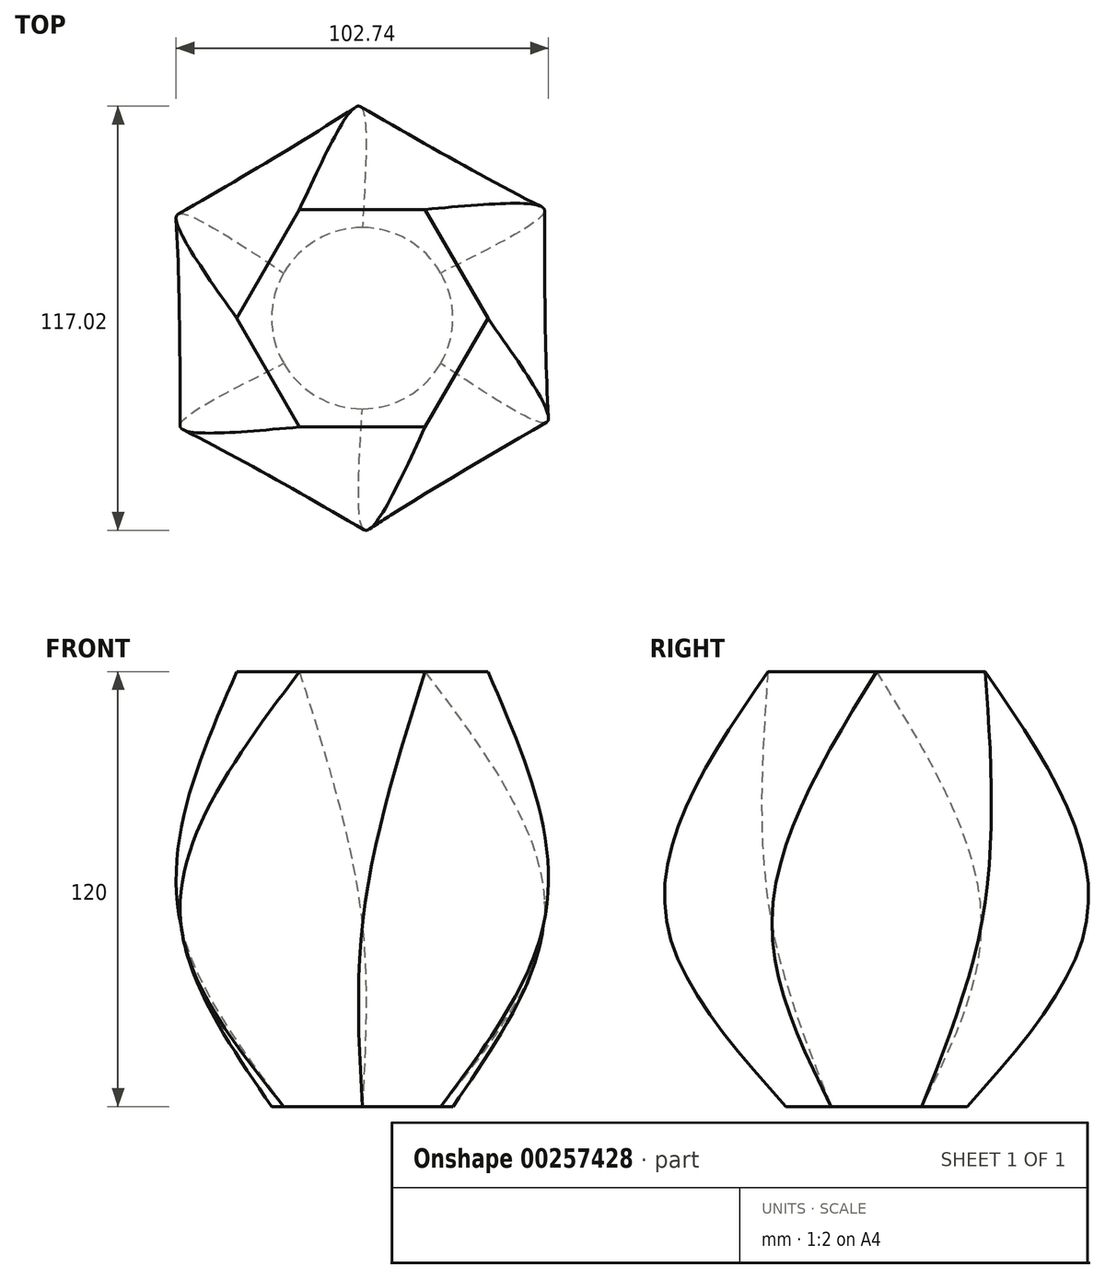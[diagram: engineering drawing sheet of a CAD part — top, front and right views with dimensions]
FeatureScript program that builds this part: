
annotation { "Feature Type Name" : "Feature", "Feature Type Description" : "" }
export const myFeature = defineFeature(function(context is Context, id is Id, definition is map)
    precondition{}
    {
        {
            var Q0;
            Q0=qCreatedBy(makeId("Top.planeOp"),FACE);
            cPlane(context, id + "F0", {"entities" : qUnion([Q0]), "cplaneType" : CPlaneType.OFFSET, "offset" : 50 * mm, "width" : 150 * mm, "height" : 150 * mm});
        }
        {
            var Q0;
            Q0=qCreatedBy(makeId("Top.planeOp"),FACE);
            cPlane(context, id + "F1", {"entities" : qUnion([Q0]), "cplaneType" : CPlaneType.OFFSET, "offset" : 120 * mm, "width" : 150 * mm, "height" : 150 * mm});
        }
        {
            var Q0;
            Q0=qCreatedBy(id+"F1.planeOp",FACE);
            var sketch = newSketch(context, id + "F2", { "sketchPlane" : qUnion([Q0])});
            skLineSegment(sketch, "E0", {"start": v(0, 52.7) * mm, "end": v(0, -45.29) * mm, "construction": true});
            skLineSegment(sketch, "E1", {"start": v(-54.44, 0) * mm, "end": v(51.9, 0) * mm, "construction": true});
            skCircle(sketch, "E2.cCircle", {"center": v(0, 0) * mm, "radius": 30 * mm, "construction": true});
            skLineSegment(sketch, "E2.0", {"start": v(17.32, -30) * mm, "end": v(-17.32, -30) * mm});
            skLineSegment(sketch, "E2.1", {"start": v(-17.32, -30) * mm, "end": v(-34.64, 0) * mm});
            skLineSegment(sketch, "E2.2", {"start": v(-34.64, 0) * mm, "end": v(-17.32, 30) * mm});
            skLineSegment(sketch, "E2.3", {"start": v(-17.32, 30) * mm, "end": v(17.32, 30) * mm});
            skLineSegment(sketch, "E2.4", {"start": v(17.32, 30) * mm, "end": v(34.64, 0) * mm});
            skLineSegment(sketch, "E2.5", {"start": v(34.64, 0) * mm, "end": v(17.32, -30) * mm});
            skPoint(sketch, "E2.0.midPoint", {"position": v(0, -30) * mm});
            skSolve(sketch);
        }
        {
            var Q0;
            Q0=qCreatedBy(id+"F0.planeOp",FACE);
            var sketch = newSketch(context, id + "F3", { "sketchPlane" : qUnion([Q0])});
            skCircle(sketch, "E3.cCircle", {"center": v(0, 0) * mm, "radius": 50 * mm, "construction": true});
            skLineSegment(sketch, "E3.0", {"start": v(50, 28.87) * mm, "end": v(50, -28.87) * mm});
            skLineSegment(sketch, "E3.1", {"start": v(50, -28.87) * mm, "end": v(0, -57.74) * mm});
            skLineSegment(sketch, "E3.2", {"start": v(0, -57.74) * mm, "end": v(-50, -28.87) * mm});
            skLineSegment(sketch, "E3.3", {"start": v(-50, -28.87) * mm, "end": v(-50, 28.87) * mm});
            skLineSegment(sketch, "E3.4", {"start": v(-50, 28.87) * mm, "end": v(0, 57.74) * mm});
            skLineSegment(sketch, "E3.5", {"start": v(0, 57.74) * mm, "end": v(50, 28.87) * mm});
            skPoint(sketch, "E3.0.midPoint", {"position": v(50, 0) * mm});
            skSolve(sketch);
        }
        {
            var Q0;
            Q0=qCreatedBy(makeId("Top.planeOp"),FACE);
            var sketch = newSketch(context, id + "F4", { "sketchPlane" : qUnion([Q0])});
            skCircle(sketch, "E4", {"center": v(0, 0) * mm, "radius": 25 * mm});
            skSolve(sketch);
        }
        {
            var Q0;
            Q0=makeQuery(id+"F2.imprint","IMPRINT",FACE,{"disambiguationData":[TD([[makeQuery(id+"F2.imprint","IMPRINT",EDGE,{"derivedFrom":sQuery(id+"F2.wireOp",EDGE,"E2.0")}),-1.0]])]});
            var Q1;
            Q1=makeQuery(id+"F3.imprint","IMPRINT",FACE,{"disambiguationData":[TD([[makeQuery(id+"F3.imprint","IMPRINT",EDGE,{"derivedFrom":sQuery(id+"F3.wireOp",EDGE,"E3.0")}),-1.0]])]});
            var Q2;
            Q2=makeQuery(id+"F4.imprint","IMPRINT",FACE,{"disambiguationData":[TD([[makeQuery(id+"F4.imprint","IMPRINT",EDGE,{"derivedFrom":sQuery(id+"F4.wireOp",EDGE,"E4")}),1.0]])]});
            loft(context, id + "F5", {"sheetProfilesArray" : [{ "sheetProfileEntities" : qUnion([Q0]) }, { "sheetProfileEntities" : qUnion([Q1]) }, { "sheetProfileEntities" : qUnion([Q2]) }]});
        }
    });
